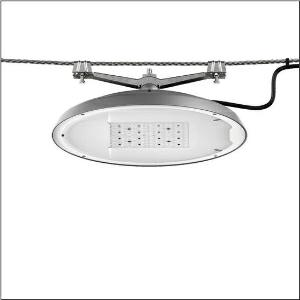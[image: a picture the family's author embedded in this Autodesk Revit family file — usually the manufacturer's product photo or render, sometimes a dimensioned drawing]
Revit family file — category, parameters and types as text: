
# Revit family: dl_r__50_iq_mini___st0_8s_5xa248v31f08le_222e
name_source: partatom
category: Lighting Fixtures
units: mm (PartAtom-declared; Revit-internal decimal feet)

## family parameters
Cut with Voids When Loaded = No
Host = Face
Light Source = No
Part Type = Normal
Room Calculation Point = No
Round Connector Dimension = Use Diameter
Shared = No

## types (1)
- --- (1 x LED, 10390 lm, 67.4 W, 3000K)
    Apparent Load = 67 VA
    CIE Flux Codes = 38 75 97 100 100
    Color Rendering = 70
    Color Temperature = 3000K
    Default Elevation = 1800 mm
    Description = DL® 50 iQ mini, catenary luminaire, primary light control with lens, of PMMA, primary optical cover: cover, of toughened safety glass, transparent, light distribution: ST0.8s, light emission: direct distribution, primary light characteristic: symmetric, installation type: suspended mounting, LED, High Power LED, rated luminous flux: 10.390lm, luminous efficacy: 154lm/W, light colour: 730, colour temperature: 3000K, control: optimised constant luminous flux control (CLO 2.0), Desk-Remote (wireless, voltage-free reading and setting of iQ features in the workshop via application-optimized NFC function/RFID function), Light-Fading, Smart-Wire, Night-Set, Lumen-Switch, Temp-Guard, Auto-Match, Street-Remote, mains connection: 230..240V, AC, 50/60Hz, start of lifetime: 67W, end of service life: 70W, reduction: 31W, luminaire housing, of diecast aluminium, powder-coated, Siteco® metallic grey (DB 702S), diameter: 500mm, height: 115mm, protection rating (complete): IP66, insulation class (complete): insulation class II (safety insulation), certification: CE, ENEC, VDE, impact resistance: IK08, permissible operating ambient temperature for outdoor applications: -25..+40°C, standard-compliant lighting for roads and squares, packaging unit: 1 piece

Light Distribution: ST0.8s
    Height = 124 mm  [stored 0.406824 ft]
    Lamp = 1 x LED
    Lamp Light Flux = 10390 lm
    Lamp Power = 67.4 W
    Lamp count = 1
    Length = 500 mm
    Luminous efficacy = 154 lm/W
    Manufacturer = Siteco
    ModVariant = No
    Model = 5XA248V31F08LE
    Number of Poles = 1
    OnlyDefault = Yes
    Power Factor = 1
    Product Name = DL® 50 iQ mini | ST0.8s
    Product group = catenary luminaire
    ProductGroupID = 6300
    Protection Class = Protection class II
    Protection Degree = IP 66
    RLX_Detail_Level = 1
    RLX_Emergency_Light_Flux = 0 lm
    RLX_Emergency_Type = 0
    RLX_Emergency_Type_DB = No
    RlxData = <blob elided: 126689 chars, md5=d52bc75b>
    Socket = socket
    Standby Power = 0 W
    System Light Flux = 10390 lm
    System Power = 67 W
    Type Comments = factory setting: luminous flux: 100 % | dim-lin: 254 | 705 mA
    Type Image = l_1251783.jpg
    URL = http://relux.com
    VarID = @adj_072383
    Voltage = 0 V
    Weight = 0.00 kg
    Width = 0 mm  [stored 0 ft]

note: [stored X ft] marks values corroborated as IEEE doubles in the binary element streams (Revit-internal decimal feet)

## geometry (parser evidence)
native form markers: Blend x4, Sweep x14
no freeform markers — native parametric forms only
